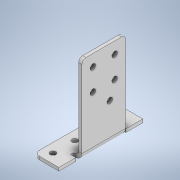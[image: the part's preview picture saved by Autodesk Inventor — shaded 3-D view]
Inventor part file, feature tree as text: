
AUTODESK INVENTOR PART (.ipt)
format: ipt  version: 2020 (Build 240168000, 168)  size: 249,856 bytes
history: native  units: mm
features: sketch x4, sheet_metal_op x2, hole x2, chamfer x2, other x2
ambient origin geometry x8: Origin, YZ Plane, XZ Plane, XY Plane, X Axis, Y Axis, Z Axis, Center Point
bodies: Solid1 (feature_tree)
feature tree (12):
  sheet_metal_op  "Face1"
  sheet_metal_op  "Fold1"
  hole  "Hole1"  [1 undecoded]
  hole  "Hole2"  [1 undecoded]
  chamfer  "Corner Round1"
  chamfer  "Corner Round2"
  sketch  "Sketch2"  dims[d7=3.0mm d8=3.0mm]
  other  "Plate1"
  sketch  "Sketch3"  dims[d9=1.5mm d10=6.0mm]
  sketch  "Sketch4"  dims[d11=3.0mm]
  sketch  "Sketch5"  dims[d12=90.0deg d13=3.0mm d14=5.1mm d15=5.1mm d16=5.1mm d17=5.1mm d18=14.0mm d19=14.0mm d20=14.0mm d21=14.0mm d22=10.0mm d23=10.0mm d24=30.0mm d25=30.0mm d26=5.1mm d27=6.0mm d28=4.0mm d29=2.0mm d30=90.0deg d31=3.0mm d32=20.594885mm d33=5.1mm d34=5.1mm d35=5.1mm d36=5.1mm d37=70.0mm d38=10.0mm d39=10.0mm d40=10.0mm d41=10.0mm d42=70.0mm d43=50.0mm d44=50.0mm d45=5.1mm d46=6.0mm d47=4.0mm d48=2.0mm d49=90.0deg d50=3.0mm d51=20.594885mm d52=3.7mm d53=4.64mm d54=22.58mm d55=77.15mm d56=18.575mm d57=18.575mm d58=20.0mm d59=20.0mm d60=78.0mm d61=5.0mm d62=14.5mm d63=35.5mm]
  other  "Definition1"
note: 2 required parameter values undecoded (feature->parameter linkage not recoverable at this tier; creation-order binding heuristic only, values carry confidence <= 0.55)
